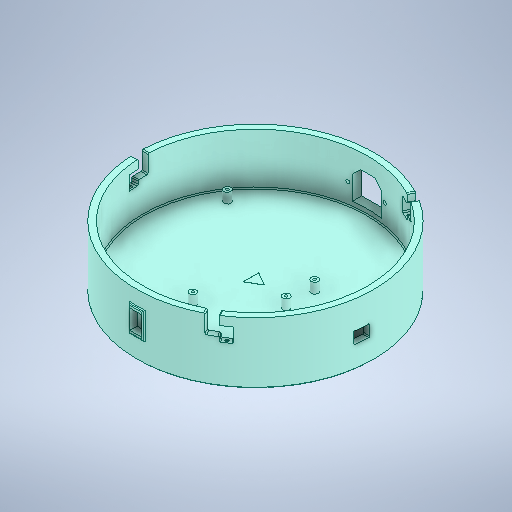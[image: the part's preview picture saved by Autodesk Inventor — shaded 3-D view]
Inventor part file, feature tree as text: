
AUTODESK INVENTOR PART (.ipt)
format: ipt  version: 2025.3 (Build 293356000, 356)  size: 649,728 bytes
history: native  units: in
note: dims shown in document units (in); Inventor stores cm internally (conversion verified against a paired STEP export)
features: sketch x16, extrude x13, plane x8, fillet x4
ambient origin geometry x8: Origin, YZ Plane, XZ Plane, XY Plane, X Axis, Y Axis, Z Axis, Center Point
bodies: Solid1 (feature_tree)
feature tree (41):
  extrude  "Extrusion1"  Depth=1.9685in TaperAngle=0.0deg
  extrude  "Extrusion2"  Depth=0.3937in TaperAngle=0.0deg
  extrude  "Extrusion9"  Depth=1.1in
  plane  "Work Plane2"
  plane  "Work Plane3"
  plane  "Work Plane4"
  sketch  "Sketch15"  dims[d118=4.375in d120=0.2835in]
  plane  "Work Plane5"
  extrude  "Extrusion13"  Depth=2.1in
  extrude  "Extrusion14"  Depth=0.1in
  fillet  "Fillet6"  Radius=0.6in
  sketch  "Sketch19"  dims[d126=0.4528in d127=0.748in d128=0.2362in d129=0.0in]
  fillet  "Fillet8"  Radius=0.1in
  extrude  "Extrusion16"  Depth=0.5264in
  extrude  "Extrusion17"  Depth=0.2835in
  plane  "Work Plane6"
  extrude  "Extrusion18"  Depth=0.5512in
  plane  "Work Plane7"
  extrude  "Extrusion19"  Depth=0.2362in TaperAngle=0.0deg
  extrude  "Extrusion20"  Depth=0.748in
  fillet  "Fillet10"  Radius=0.2362in
  plane  "Work Plane10"
  extrude  "Extrusion22"  Depth=0.0394in
  plane  "Work Plane11"
  extrude  "Extrusion23"  Depth=0.1102in
  extrude  "Extrusion24"  Depth=0.1417in
  fillet  "Fillet11"  Radius=0.1102in
  sketch  "Sketch1"  dims[d0=8.6614in d1=1.9685in d2=0.0in]
  sketch  "Sketch2"  dims[d3=9.1339in d4=0.3937in d5=0.0in]
  sketch  "Sketch11"  dims[d107=0.1in d108=0.5264in]
  sketch  "Sketch17"  dims[d121=0.2047in d122=0.5512in]
  sketch  "Sketch18"  dims[d123=0.9843in d124=0.2362in d125=0.0in]
  sketch  "Sketch20"  dims[d130=0.0394in d132=3.0709in]
  sketch  "Sketch22"  dims[d133=4.3701in d137=0.1102in]
  sketch  "Sketch23"  dims[d138=0.1575in d139=0.1417in d140=0.1102in]
  sketch  "Sketch28"  dims[d141=0.1575in]
  sketch  "Sketch Circular Pattern2"  dims[d73=0.0039in d74=0.0in d100=1.1in]
  sketch  "Sketch29"  dims[d142=0.1417in]
  sketch  "Sketch Circular Pattern3"  dims[d101=2.7in d102=2.1in]
  sketch  "Sketch30"  dims[d150=0.0394in d156=1.2598in d157=0.1102in d158=0.1102in d159=0.1102in d160=0.1102in d161=0.2756in d162=0.2756in d163=0.2756in d164=0.2756in d165=0.3937in d166=0.0in d167=0.2756in d168=0.2756in d169=0.3937in d170=0.0in d171=4.0625in d172=0.0394in d173=0.5709in d174=0.4528in d175=0.3937in d176=0.0in d177=0.1575in d178=0.4528in d179=0.3937in d180=-4.375in d181=1.122in d182=0.9055in d184=0.2756in d187=0.5512in d188=0.1969in d189=0.7874in d190=0.2815in d191=0.0in d192=0.1339in d193=0.1339in d194=0.5906in d195=1.4173in d196=0.7087in d197=0.4798in d198=0.7087in d199=0.0in d200=0.0in d201=0.0394in d219=0.0344in d220=0.0172in d221=1.1811in d223=360.0deg d225=0.0in d226=0.7087in d227=0.0in d228=-0.3346in d229=0.0344in d230=0.0172in d231=0.0in d232=0.5512in d233=0.0in d234=1.1811in d236=360.0deg d238=8.8976in d239=0.0515in d240=0.1181in d241=1.1811in d243=360.0deg d245=0.0394in d246=0.0in d247=0.0394in d151=0.0in d152=0.0in d153=0.0in]
  sketch  "Sketch Circular Pattern4"  dims[d103=0.7in d104=0.1in d105=0.6in d106=0.1in]
